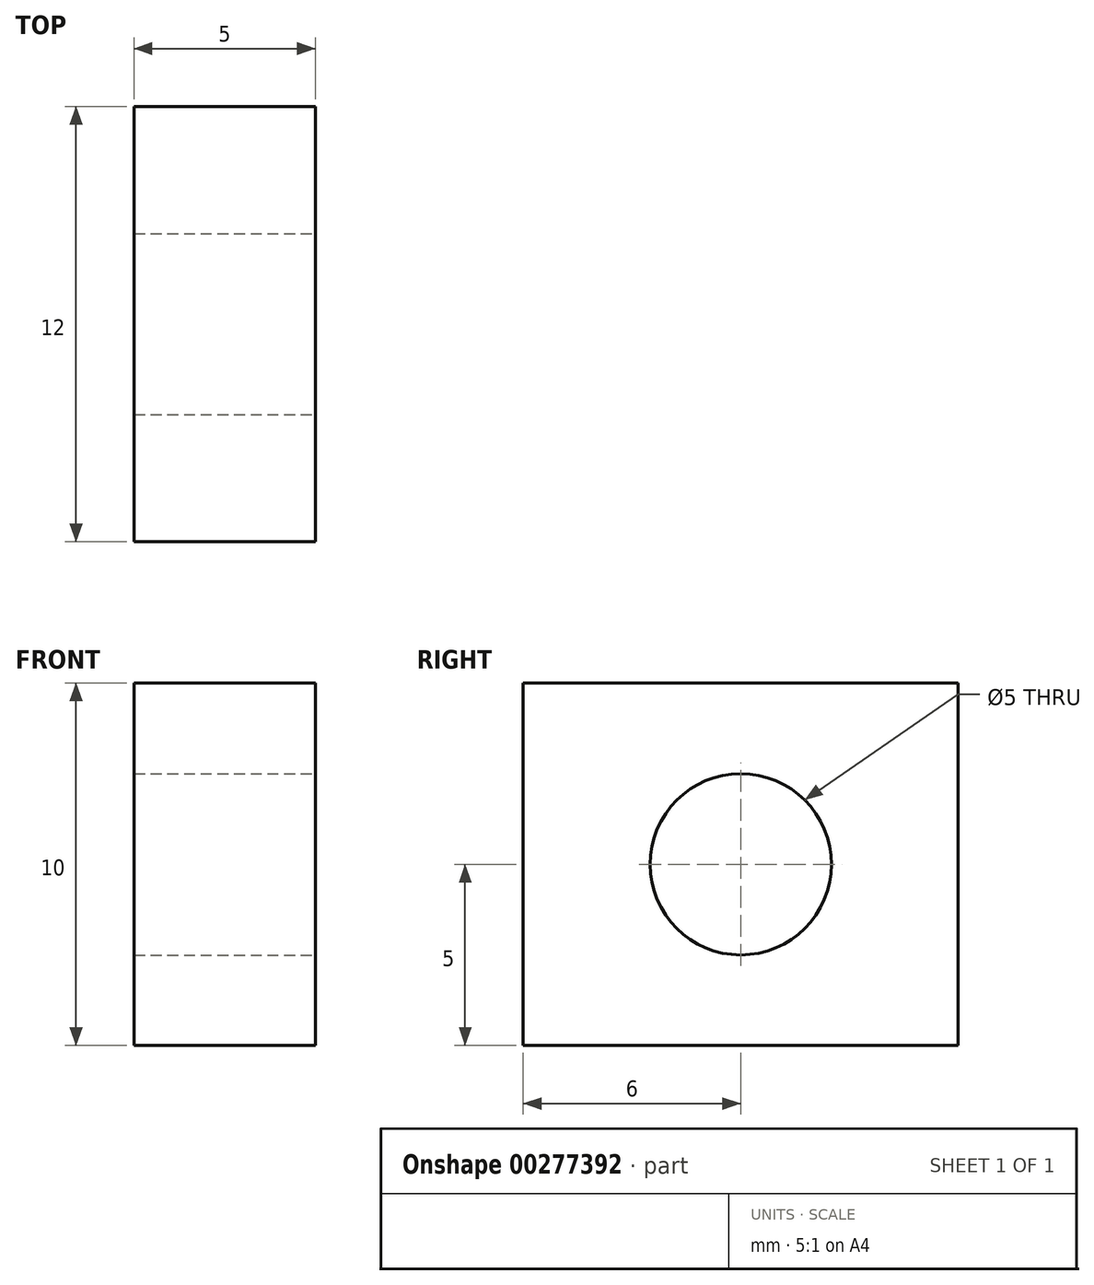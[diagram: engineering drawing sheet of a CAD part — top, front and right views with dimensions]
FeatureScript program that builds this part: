
annotation { "Feature Type Name" : "Feature", "Feature Type Description" : "" }
export const myFeature = defineFeature(function(context is Context, id is Id, definition is map)
    precondition{}
    {
        {
            var Q0;
            Q0=qCreatedBy(makeId("Top.planeOp"),FACE);
            var sketch = newSketch(context, id + "F0", { "sketchPlane" : qUnion([Q0])});
            skLineSegment(sketch, "E0.bottom", {"start": v(0, 0) * mm, "end": v(5, 0) * mm});
            skLineSegment(sketch, "E0.top", {"start": v(0, 12) * mm, "end": v(5, 12) * mm});
            skLineSegment(sketch, "E0.left", {"start": v(0, 0) * mm, "end": v(0, 12) * mm});
            skLineSegment(sketch, "E0.right", {"start": v(5, 0) * mm, "end": v(5, 12) * mm});
            skSolve(sketch);
        }
        {
            var Q0;
            Q0 = qSketchRegion(id + "F0", true);
            extrude(context, id + "F1", {"entities" : qUnion([Q0]), "depth" : 10 * mm});
        }
        {
            var Q0;
            Q0=makeQuery(id+"F1.opExtrude","SWEPT_FACE",FACE,{"disambiguationData":[OSD([sQuery(id+"F0.wireOp",EDGE,"E0.right")])]});
            var sketch = newSketch(context, id + "F2", { "sketchPlane" : qUnion([Q0])});
            skCircle(sketch, "E1", {"center": v(6, 5) * mm, "radius": 2.5 * mm});
            skSolve(sketch);
        }
        {
            var Q0;
            Q0=sQuery(id+"F2.wireOp",VERTEX,"E1.center");
            var Q1;
            Q1=makeQuery(id+"F1.opExtrude","SWEPT_BODY",BODY,{"disambiguationData":[OSD([sQuery(id+"F0.wireOp",EDGE,"E0.bottom"),sQuery(id+"F0.wireOp",EDGE,"E0.top"),sQuery(id+"F0.wireOp",EDGE,"E0.left"),sQuery(id+"F0.wireOp",EDGE,"E0.right")])]});
            hole(context, id + "F3", {"style" : HoleStyle.SIMPLE, "endStyle" : HoleEndStyle.THROUGH, "holeDiameter" : 5 * mm, "tappedDepth" : 12.7 * mm, "tapClearance" : 3, "locations" : qUnion([Q0]), "scope" : qUnion([Q1])});
        }
    });
